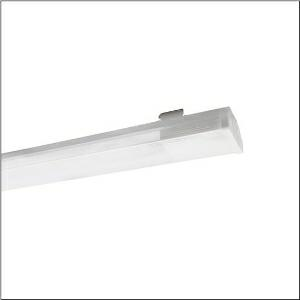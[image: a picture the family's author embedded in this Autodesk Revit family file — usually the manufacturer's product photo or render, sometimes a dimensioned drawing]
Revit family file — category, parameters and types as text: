
# Revit family: modario_r__31_gen_2_53bm811du4l3d2_a34c
name_source: partatom
category: Lighting Fixtures
units: mm (PartAtom-declared; Revit-internal decimal feet)

## family parameters
Cut with Voids When Loaded = No
Host = Face
Light Source = No
Part Type = Normal
Room Calculation Point = No
Round Connector Dimension = Use Diameter
Shared = No

## types (1)
- --- (1 x LED, 23600 lm, 128.4 W, 4000K)
    Apparent Load = 128 VA
    CIE Flux Codes = 50 78 94 90 100
    Color Rendering = 80
    Color Temperature = 4000K
    Default Elevation = 1800 mm
    Description = Modario® 31 Gen.2, luminaire insert, of sheet steel, coil coated, white, length: 2.392mm, width: 81mm, height: 82mm, 8x system unit, system units: 299mm, LED rated luminous flux: 23.600lm, light colour: 840, control gear: DALI 2, control gear: ECG DALI, with plug, 5-pole, with phase selection, mains connection: 220..240V, AC, 50/60Hz, rated input power: 128W, through-wiring accessed according to module size, primary optical cover: cover, of PMMA, light emission: direct distribution, primary light characteristic: symmetric, protection rating (complete): IP20, protection rating (LED compartment): IP50, insulation class (complete): insulation class I (protective earthing), certification: CE, ENEC, VDE, UKCA, impact resistance: IK03, permissible ambient temperature for indoor applications: -40..+35°C, corresponds to IFS (International Featured Standards) requirements for safety and quality in the food industry, reducing of maximum allowable ambient temperature of 5°C with ceiling mounting, packaging unit: 1 piece
    Height = 92 mm
    Lamp = 1 x LED
    Lamp Light Flux = 23600 lm
    Lamp Power = 128.4 W
    Lamp count = 1
    Length = 2392 mm
    Luminous efficacy = 184 lm/W
    Manufacturer = Siteco
    ModVariant = No
    Model = 53BM811DU4L3D2
    Mounting Place = Ceiling
    Mounting Type = Pendant
    Number of Poles = 1
    OnlyDefault = Yes
    Power Factor = 1
    Product Name = Modario® 31 Gen.2
    Product group = luminaire insert | ceiling pendant
    ProductGroupID = 902
    Protection Class = Protection class I
    Protection Degree = IP 20
    RLX_Detail_Level = 1
    RLX_Emergency_Light_Flux = 0 lm
    RLX_Emergency_Type = 0
    RLX_Emergency_Type_DB = No
    RlxData = <blob elided: 38525 chars, md5=fc0fa80a>
    Socket = socket
    Standby Power = 0 W
    System Light Flux = 23600 lm
    System Power = 128 W
    Type Comments = factory setting: luminous flux: 100 % | dim-lin: 254 | 594 mA
    Type Image = l_1341883.jpg
    URL = http://relux.com
    VarID = @adj_064713
    Voltage = 0 V
    Weight = 0.00 kg
    Width = 81 mm

## geometry (parser evidence)
native form markers: Blend x4, Sweep x14
no freeform markers — native parametric forms only
